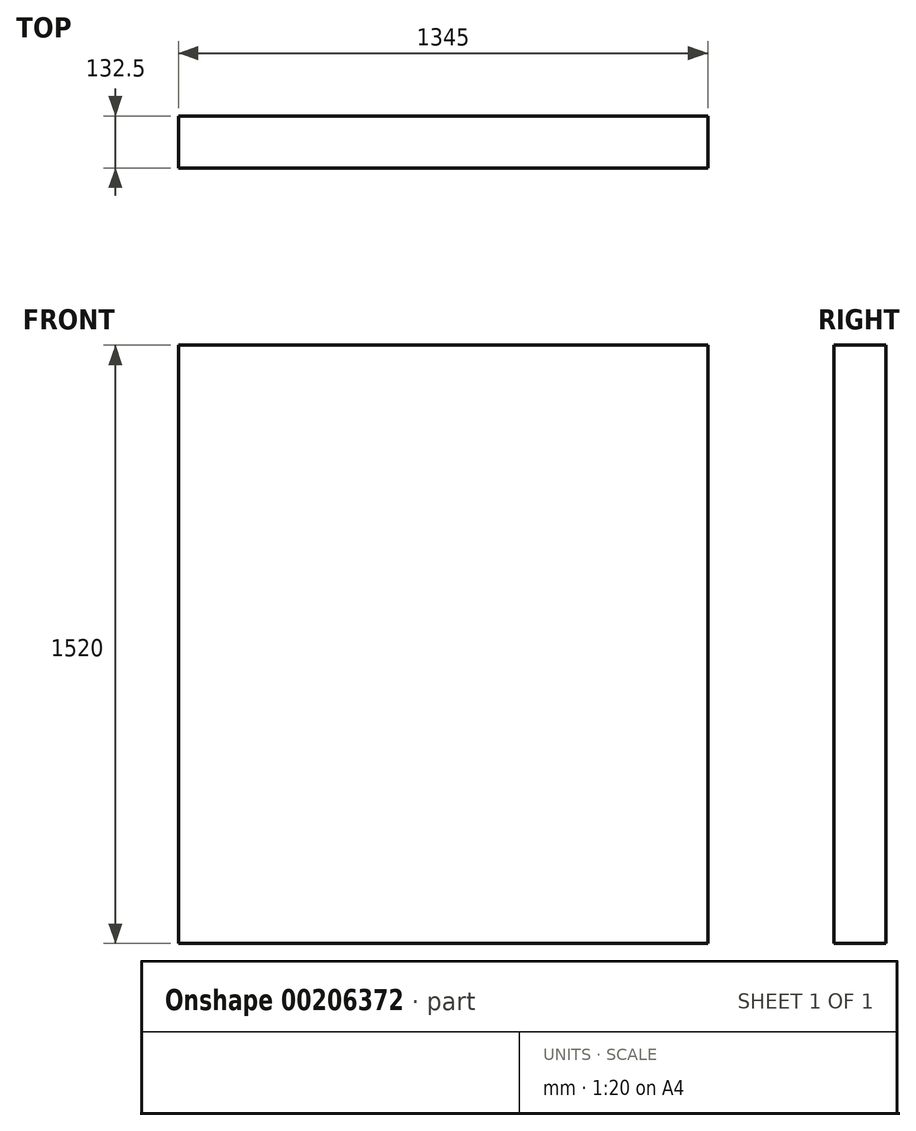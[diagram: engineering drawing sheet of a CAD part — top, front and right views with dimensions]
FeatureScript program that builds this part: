
annotation { "Feature Type Name" : "Feature", "Feature Type Description" : "" }
export const myFeature = defineFeature(function(context is Context, id is Id, definition is map)
    precondition{}
    {
        {
            var Q0;
            Q0=qCreatedBy(makeId("Front.planeOp"),FACE);
            var sketch = newSketch(context, id + "F0", { "sketchPlane" : qUnion([Q0])});
            skLineSegment(sketch, "E0.bottom", {"start": v(-670.52, -90.9) * mm, "end": v(674.48, -90.9) * mm});
            skLineSegment(sketch, "E0.top", {"start": v(-670.52, 1429.1) * mm, "end": v(674.48, 1429.1) * mm});
            skLineSegment(sketch, "E0.left", {"start": v(-670.52, -90.9) * mm, "end": v(-670.52, 1429.1) * mm});
            skLineSegment(sketch, "E0.right", {"start": v(674.48, -90.9) * mm, "end": v(674.48, 1429.1) * mm});
            skSolve(sketch);
        }
        {
            var Q0;
            Q0=makeQuery(id+"F0.imprint","IMPRINT",FACE,{"disambiguationData":[TD([[makeQuery(id+"F0.imprint","IMPRINT",EDGE,{"derivedFrom":sQuery(id+"F0.wireOp",EDGE,"E0.bottom")}),1.0]])]});
            extrude(context, id + "F1", {"entities" : qUnion([Q0]), "depth" : 132.5 * mm});
        }
    });
